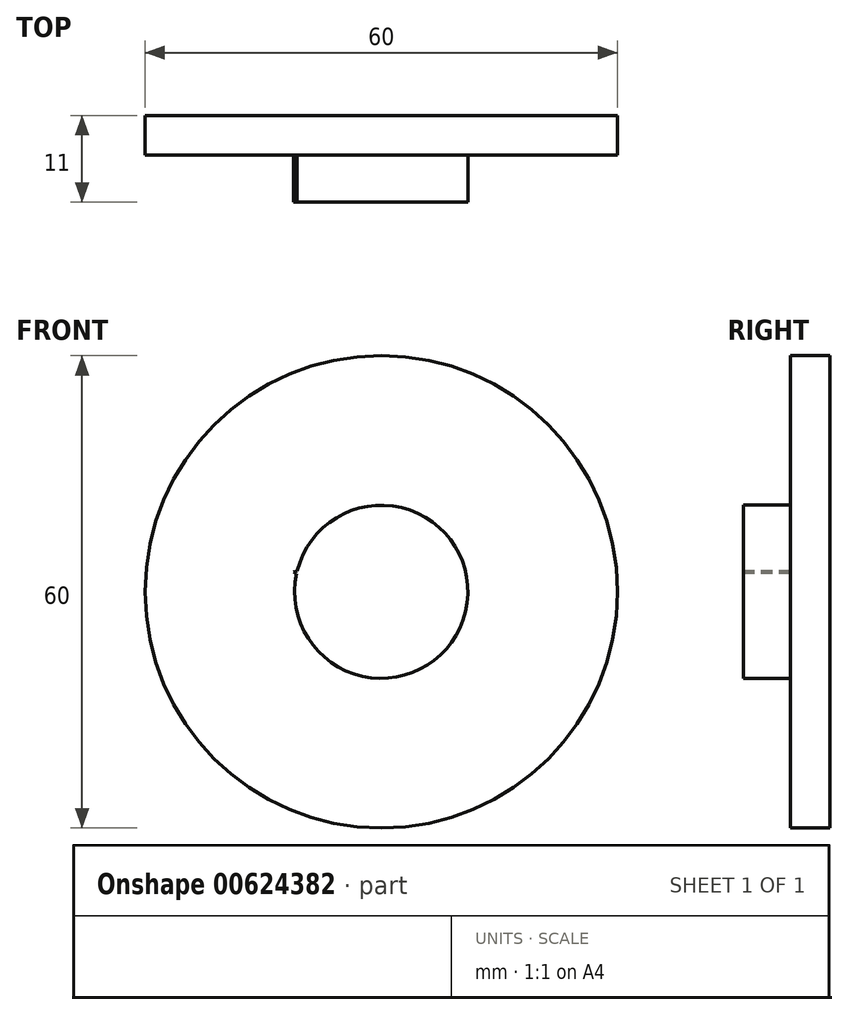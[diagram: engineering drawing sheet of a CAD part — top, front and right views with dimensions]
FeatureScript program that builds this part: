
annotation { "Feature Type Name" : "Feature", "Feature Type Description" : "" }
export const myFeature = defineFeature(function(context is Context, id is Id, definition is map)
    precondition{}
    {
        {
            var Q0;
            Q0=qCreatedBy(makeId("Front.planeOp"),FACE);
            var sketch = newSketch(context, id + "F0", { "sketchPlane" : qUnion([Q0])});
            skCircle(sketch, "E0", {"center": v(0, 0) * mm, "radius": 30 * mm});
            skSolve(sketch);
        }
        {
            var Q0;
            Q0=qCreatedBy(makeId("Front.planeOp"),FACE);
            var sketch = newSketch(context, id + "F1", { "sketchPlane" : qUnion([Q0])});
            skCircle(sketch, "E1", {"center": v(0, 0) * mm, "radius": 11 * mm});
            skSolve(sketch);
        }
        {
            var Q0;
            Q0 = qSketchRegion(id + "F1", true);
            extrude(context, id + "F2", {"entities" : qUnion([Q0]), "depth" : 11 * mm, "offsetDistance" : 25 * mm});
        }
        {
            var Q0;
            Q0=makeQuery(id+"F0.imprint","IMPRINT",FACE,{"disambiguationData":[TD([[makeQuery(id+"F0.imprint","IMPRINT",EDGE,{"derivedFrom":sQuery(id+"F0.wireOp",EDGE,"E0")}),1.0]])]});
            extrude(context, id + "F3", {"entities" : qUnion([Q0]), "operationType" : NewBodyOperationType.ADD, "depth" : 5 * mm, "offsetDistance" : 25 * mm});
        }
        {
            var Q0;
            Q0=makeQuery(id+"F2.opExtrude","CAP_FACE",FACE,{"disambiguationData":[OSD([sQuery(id+"F1.wireOp",EDGE,"E1")])],"isStart":false});
            var sketch = newSketch(context, id + "F4", { "sketchPlane" : qUnion([Q0])});
            skLineSegment(sketch, "E2", {"start": v(-10.75, 2.33) * mm, "end": v(-11.13, 2.54) * mm});
            skLineSegment(sketch, "E3", {"start": v(-11.13, 2.53) * mm, "end": v(-10.68, 2.65) * mm});
            skLineSegment(sketch, "E4", {"start": v(-10.68, 2.65) * mm, "end": v(-10.75, 2.33) * mm});
            skSolve(sketch);
        }
        {
            var Q0;
            {var subQ0=sQuery(id+"F4.wireOp",EDGE,"E2");Q0=makeQuery(id+"F4.imprint","IMPRINT",FACE,{"disambiguationData":[TD([[makeQuery(id+"F4.imprint","IMPRINT",EDGE,{"derivedFrom":subQ0}),-1.0]])]});}
            extrude(context, id + "F5", {"entities" : qUnion([Q0]), "operationType" : NewBodyOperationType.ADD, "oppositeDirection" : true, "depth" : 6.3 * mm, "offsetDistance" : 25 * mm});
        }
    });
